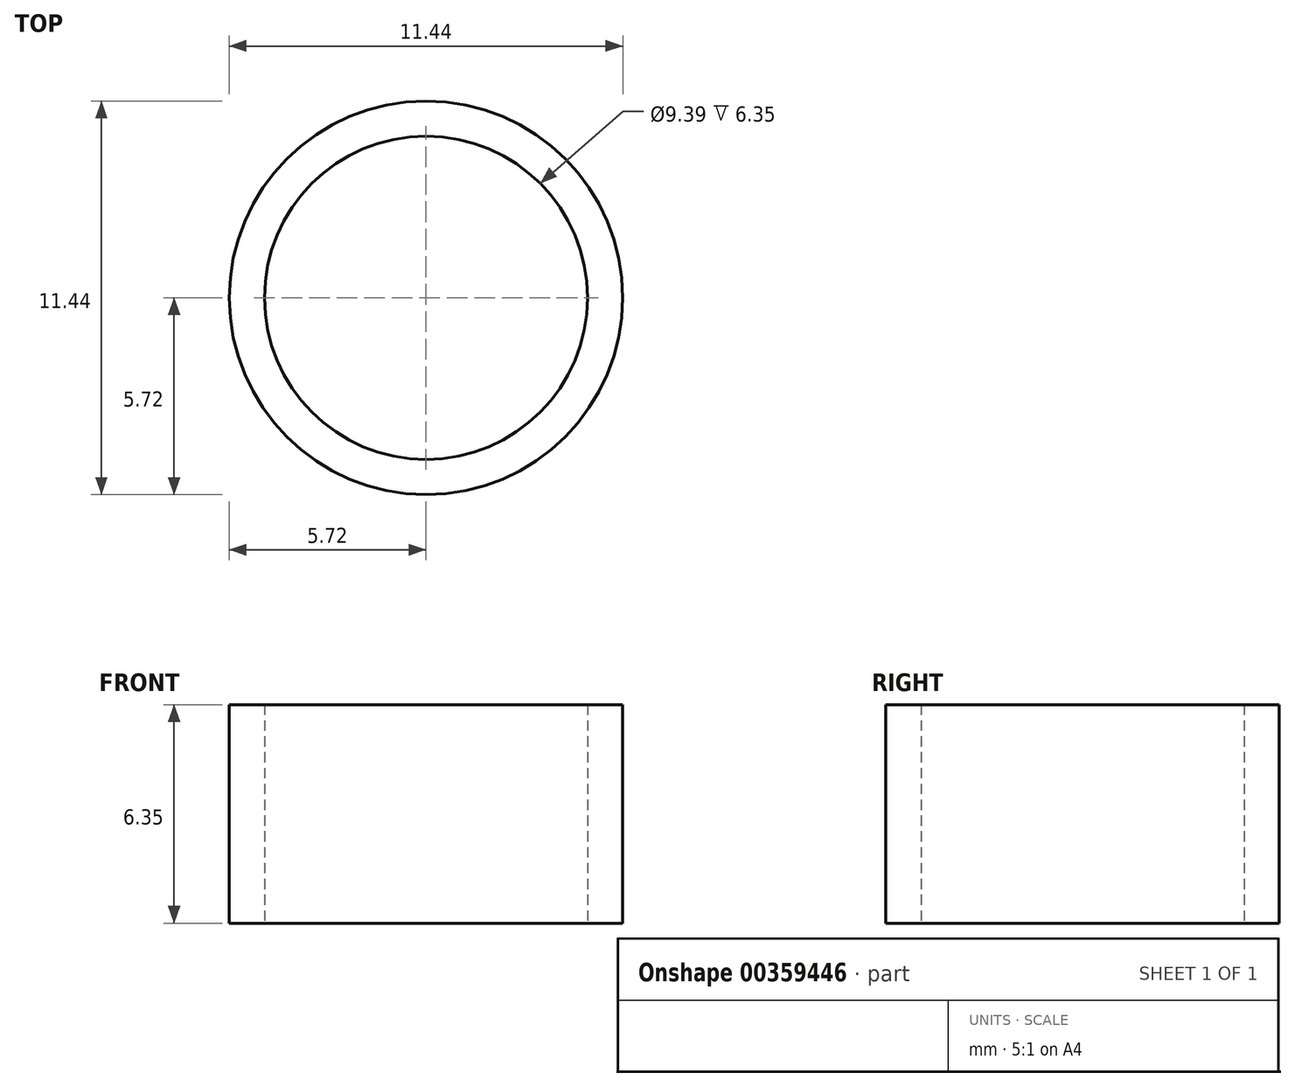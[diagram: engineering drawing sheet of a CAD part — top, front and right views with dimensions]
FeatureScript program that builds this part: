
annotation { "Feature Type Name" : "Feature", "Feature Type Description" : "" }
export const myFeature = defineFeature(function(context is Context, id is Id, definition is map)
    precondition{}
    {
        {
            var Q0;
            Q0=qCreatedBy(makeId("Top.planeOp"),FACE);
            var sketch = newSketch(context, id + "F0", { "sketchPlane" : qUnion([Q0])});
            skCircle(sketch, "E0", {"center": v(0, 0) * mm, "radius": 4.7 * mm});
            skCircle(sketch, "E1", {"center": v(0, 0) * mm, "radius": 5.72 * mm});
            skSolve(sketch);
        }
        {
            var Q0;
            Q0 = qSketchRegion(id + "F0", true);
            extrude(context, id + "F1", {"entities" : qUnion([Q0]), "depth" : 6.35 * mm});
        }
    });
